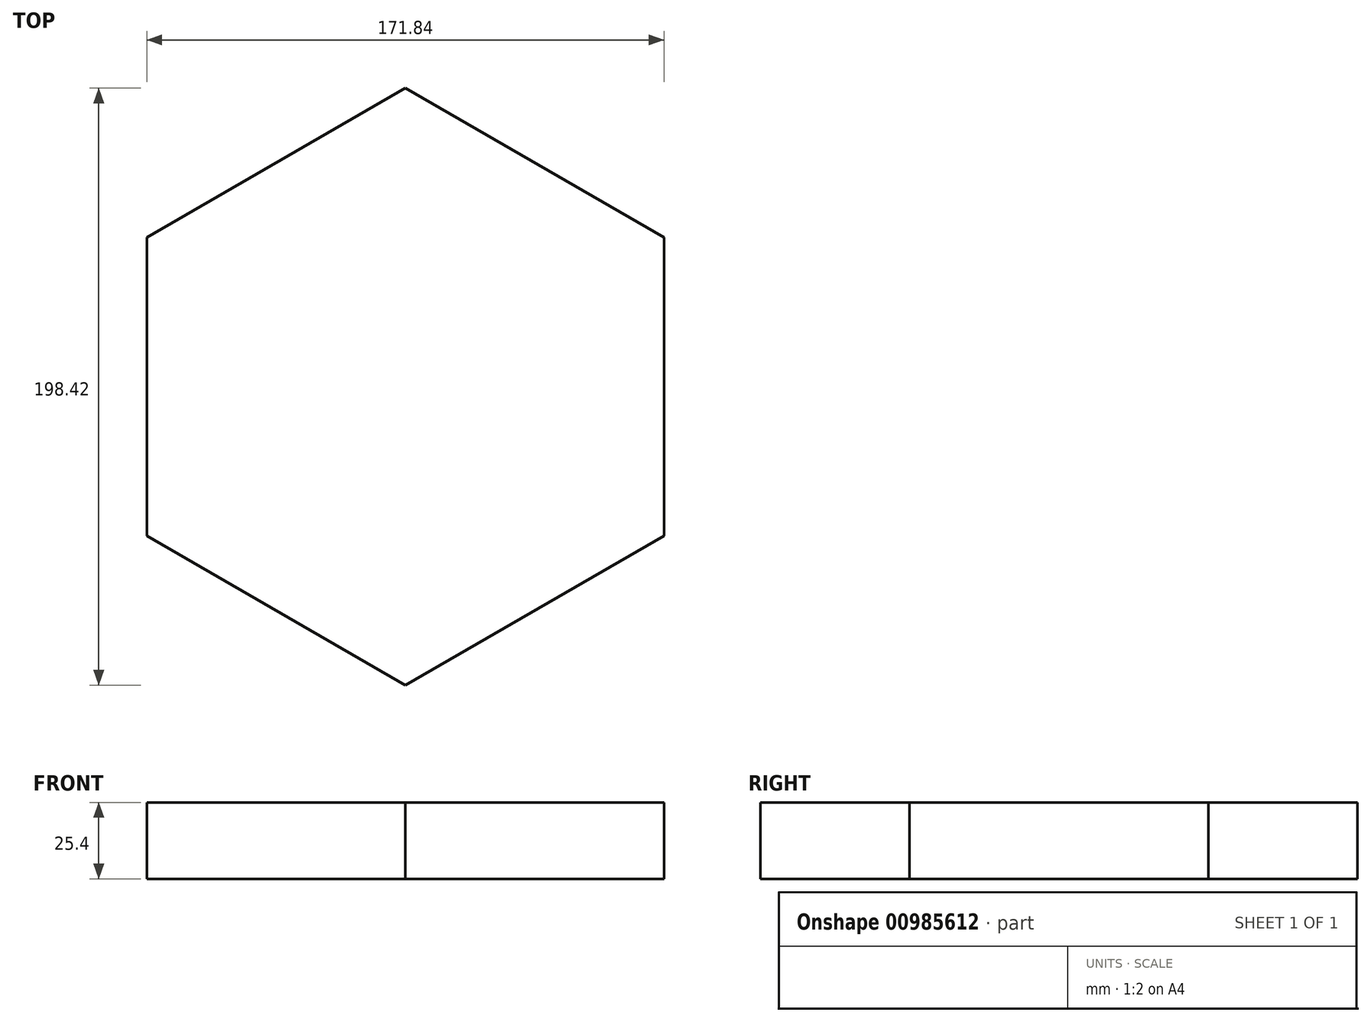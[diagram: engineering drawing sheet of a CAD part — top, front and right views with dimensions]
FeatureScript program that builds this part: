
annotation { "Feature Type Name" : "Feature", "Feature Type Description" : "" }
export const myFeature = defineFeature(function(context is Context, id is Id, definition is map)
    precondition{}
    {
        {
            var Q0;
            Q0=qCreatedBy(makeId("Top.planeOp"),FACE);
            var sketch = newSketch(context, id + "F0", { "sketchPlane" : qUnion([Q0])});
            skCircle(sketch, "E0.cCircle", {"center": v(0, 0) * mm, "radius": 85.92 * mm, "construction": true});
            skLineSegment(sketch, "E0.0", {"start": v(85.92, 49.6) * mm, "end": v(85.92, -49.6) * mm});
            skLineSegment(sketch, "E0.1", {"start": v(85.92, -49.6) * mm, "end": v(0, -99.2) * mm});
            skLineSegment(sketch, "E0.2", {"start": v(0, -99.2) * mm, "end": v(-85.92, -49.6) * mm});
            skLineSegment(sketch, "E0.3", {"start": v(-85.92, -49.6) * mm, "end": v(-85.92, 49.6) * mm});
            skLineSegment(sketch, "E0.4", {"start": v(-85.92, 49.6) * mm, "end": v(0, 99.2) * mm});
            skLineSegment(sketch, "E0.5", {"start": v(0, 99.2) * mm, "end": v(85.92, 49.6) * mm});
            skPoint(sketch, "E0.0.midPoint", {"position": v(85.92, 0) * mm});
            skSolve(sketch);
        }
        {
            var Q0;
            Q0=makeQuery(id+"F0.imprint","IMPRINT",FACE,{"disambiguationData":[TD([[makeQuery(id+"F0.imprint","IMPRINT",EDGE,{"derivedFrom":sQuery(id+"F0.wireOp",EDGE,"E0.0")}),-1.0]])]});
            var Q1;
            Q1 = qSketchRegion(id + "F0", true);
            extrude(context, id + "F1", {"entities" : qUnion([Q0, Q1]), "depth" : 25.4 * mm, "offsetDistance" : 25.4 * mm});
        }
    });
